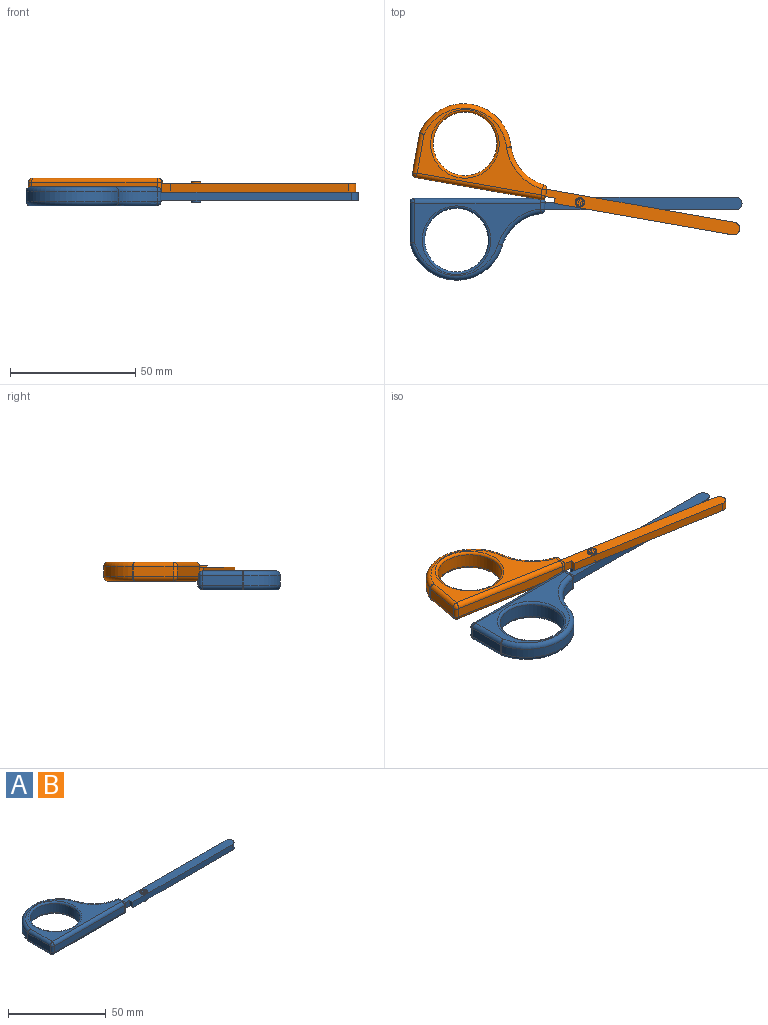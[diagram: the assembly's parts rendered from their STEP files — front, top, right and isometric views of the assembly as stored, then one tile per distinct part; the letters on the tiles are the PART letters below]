
ASSEMBLY  parts=2 mates=1
PART A: 63 faces, bbox 134.1x34.8x7.6 mm
  f0: plane 2.94x0.19mm, normal (1,0.03,0), area 0.6mm2, adj f2,f11,f20,f25
  f1: plane 2.94x0.19mm, normal (1,0.03,0), area 0.6mm2, adj f2,f11,f19,f35
  f2: cylinder r=1.52mm len=3.94mm, axis (0,0,-1), area 8.6mm2, adj f0,f1,f3,f14,f27,f37
  f3: cylinder r=18.67mm len=15.56mm, axis (0,0,-1), area 83.5mm2, adj f2,f4,f29,f39
  f4: cylinder r=1.52mm len=3.94mm, axis (0,0,-1), area 0.3mm2, adj f3,f5,f30,f40
  f5: cylinder r=19.05mm len=36.88mm, axis (0,0,-1), area 197.9mm2, adj f4,f6,f28,f38
  f6: cylinder r=1.52mm len=3.94mm, axis (0,0,-1), area 1.4mm2, adj f5,f7,f26,f36
  f7: plane 16.08x3.94mm, normal (-1,0,0), area 63.4mm2, adj f6,f8,f24,f34
  f8: cylinder r=1.52mm len=3.94mm, axis (0,0,-1), area 9.4mm2, adj f7,f9,f22,f32
  f9: plane 50.89x3.94mm, normal (0,-1,0), area 200.5mm2, adj f8,f11,f21,f31
  f10: cylinder r=12.7mm len=25.4mm, axis (0,0,-1), area 451.5mm2, adj f41,f42
  f11: cylinder r=1.52mm len=3.94mm, axis (0,0,-1), area 9.6mm2, adj f0,f1,f9,f15,f23,f33
  f12: plane 50.25x28.95mm, normal (0,0,1), area 375.7mm2, adj f31,f34,f35,f38,f39,f40,f42
  f13: plane 50.25x28.95mm, normal (0,0,-1), area 375.7mm2, adj f21,f24,f25,f28,f29,f30,f41
  f14: plane 76.2x3.56mm, normal (0,1,0), area 271mm2, adj f2,f18,f19,f20
  f15: plane 3.84x3.56mm, normal (0,-1,0), area 13.6mm2, adj f11,f16,f19,f20
  f16: plane 3.56x2.14mm, normal (-1,0,0), area 7.6mm2, adj f15,f17,f19,f20
  f17: plane 72.29x3.56mm, normal (0,-1,0), area 257.1mm2, adj f16,f18,f19,f20
  f18: cylinder r=2.54mm len=5.08mm, axis (0,0,-1), area 28.4mm2, adj f14,f17,f19,f20
  f19: plane 78.74x5.08mm, normal (0,0,1), area 377.5mm2, adj f1,f14,f15,f16,f17,f18,f47
  f20: plane 78.74x5.08mm, normal (0,0,-1), area 377.5mm2, adj f0,f14,f15,f16,f17,f18,f45
  f21: cylinder r=1.84mm len=50.89mm, axis (1,0,0), area 146.4mm2, adj f9,f13,f22,f23
  f22: bspline ~2.27x1.84mm, area 4.5mm2, adj f8,f21,f24
  f23: bspline ~2.28x1.89mm, area 4.6mm2, adj f11,f21,f25
  f24: cylinder r=1.84mm len=16.08mm, axis (0,-1,0), area 46.1mm2, adj f7,f13,f22,f26
  f25: cylinder r=1.84mm len=2.98mm, axis (-0.03,1,0), area 7.9mm2, adj f0,f13,f23,f27
  f26: bspline ~1.84x1.84mm, area 0.7mm2, adj f6,f24,f28
  f27: bspline ~2.38x1.83mm, area 4.1mm2, adj f2,f25,f29
  f28: torus R=17.21mm, axis (0,0,1), area 140mm2, adj f5,f13,f26,f30
  f29: torus R=20.51mm, axis (0,0,1), area 63.1mm2, adj f3,f13,f27,f30
  f30: torus R=3.36mm, axis (0,0,1), area 0.3mm2, adj f4,f13,f28,f29
  f31: cylinder r=1.84mm len=50.89mm, axis (-1,0,0), area 146.4mm2, adj f9,f12,f32,f33
  f32: bspline ~2.27x1.84mm, area 4.5mm2, adj f8,f31,f34
  f33: bspline ~2.28x1.89mm, area 4.6mm2, adj f11,f31,f35
  f34: cylinder r=1.84mm len=16.08mm, axis (0,1,0), area 46.1mm2, adj f7,f12,f32,f36
  f35: cylinder r=1.84mm len=2.98mm, axis (0.03,-1,0), area 7.9mm2, adj f1,f12,f33,f37
  f36: bspline ~1.84x1.84mm, area 0.7mm2, adj f6,f34,f38
  f37: bspline ~2.38x1.83mm, area 4.1mm2, adj f2,f35,f39
  f38: torus R=17.21mm, axis (0,0,1), area 140mm2, adj f5,f12,f36,f40
  f39: torus R=20.51mm, axis (0,0,1), area 63.1mm2, adj f3,f12,f37,f40
  f40: torus R=3.36mm, axis (0,0,1), area 0.3mm2, adj f4,f12,f38,f39
  f41: torus R=13.68mm, axis (0,0,1), area 126.4mm2, adj f10,f13
  f42: torus R=13.68mm, axis (0,0,1), area 126.4mm2, adj f10,f12
  f43: cylinder r=1.71mm len=3.43mm, axis (0,0,-1), area 2.7mm2, adj f44,f55
  f44: plane 3.78x3.78mm, normal (0,0,-1), area 2mm2, adj f43,f45
  f45: cylinder r=1.89mm len=3.78mm, axis (0,0,-1), area 9mm2, adj f20,f44
  f46: cylinder r=1.71mm len=3.43mm, axis (0,0,-1), area 2.7mm2, adj f48,f62
  f47: cylinder r=1.89mm len=3.78mm, axis (0,0,-1), area 9mm2, adj f19,f48
  f48: plane 3.78x3.78mm, normal (0,0,1), area 2mm2, adj f46,f47
  f49: plane 3.13x0.81mm, normal (0,0,-1), area 1.8mm2, adj f51,f52
  f50: plane 3.13x0.81mm, normal (0,0,-1), area 1.8mm2, adj f53,f54
  f51: plane 3.13x0.19mm, normal (1,0,0), area 0.6mm2, adj f49,f52,f55
  f52: cylinder r=1.92mm len=3.13mm, axis (0,0,-1), area 0.7mm2, adj f49,f51,f55
  f53: cylinder r=1.92mm len=3.13mm, axis (0,0,-1), area 0.7mm2, adj f50,f54,f55
  f54: plane 3.13x0.19mm, normal (-1,0,0), area 0.6mm2, adj f50,f53,f55
  f55: plane 3.43x3.43mm, normal (0,0,-1), area 5.7mm2, adj f43,f51,f52,f53,f54
  f56: plane 3.13x0.81mm, normal (0,0,1), area 1.8mm2, adj f58,f59
  f57: plane 3.13x0.81mm, normal (0,0,1), area 1.8mm2, adj f60,f61
  f58: plane 3.13x0.19mm, normal (1,0,0), area 0.6mm2, adj f56,f59,f62
  f59: cylinder r=1.92mm len=3.13mm, axis (0,0,-1), area 0.7mm2, adj f56,f58,f62
  f60: cylinder r=1.92mm len=3.13mm, axis (0,0,-1), area 0.7mm2, adj f57,f61,f62
  f61: plane 3.13x0.19mm, normal (-1,0,0), area 0.6mm2, adj f57,f60,f62
  f62: plane 3.43x3.43mm, normal (0,0,1), area 5.7mm2, adj f46,f58,f59,f60,f61
PART B: same geometry as A
PLACE A rot(axis=(1,0,0),180deg) t=(10.41,-9.27,-0.26)mm
PLACE B rot(axis=(0,0,-1),10deg) t=(10.28,-10.68,3.29)mm
MATE revolute A.f43 <-> B.f43  axis (0,0,1) through (20.48,-10.86,1.51)mm
